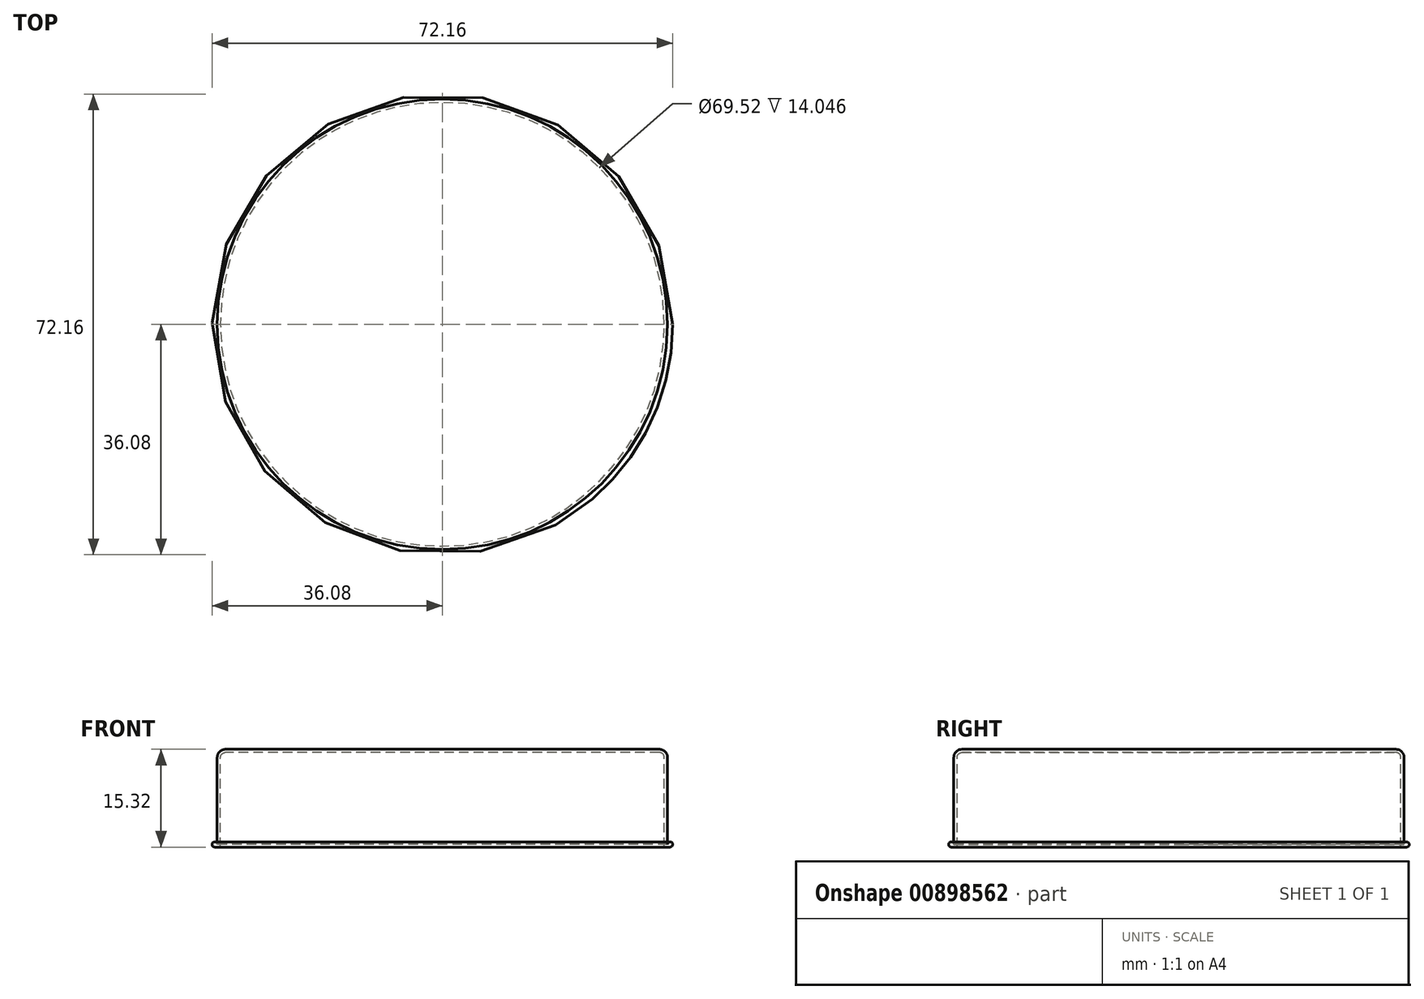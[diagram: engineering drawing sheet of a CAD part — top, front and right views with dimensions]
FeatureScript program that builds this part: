
annotation { "Feature Type Name" : "Feature", "Feature Type Description" : "" }
export const myFeature = defineFeature(function(context is Context, id is Id, definition is map)
    precondition{}
    {
        {
            var Q0;
            Q0=qCreatedBy(makeId("Front.planeOp"),FACE);
            var sketch = newSketch(context, id + "F0", { "sketchPlane" : qUnion([Q0])});
            skLineSegment(sketch, "E0", {"start": v(0, 0) * mm, "end": v(34, 0) * mm});
            skLineSegment(sketch, "E1", {"start": v(35.27, -1.27) * mm, "end": v(35.27, -14.9) * mm});
            skLineSegment(sketch, "E2.0", {"start": v(34.76, -1.27) * mm, "end": v(34.76, -15.32) * mm});
            skLineSegment(sketch, "E2.1", {"start": v(0, -0.5) * mm, "end": v(34, -0.5) * mm});
            skPoint(sketch, "E3.orphan", {"position": v(-76.06, 0) * mm});
            skLineSegment(sketch, "E4", {"start": v(35.67, -15.32) * mm, "end": v(34.76, -15.32) * mm});
            skArc(sketch, "E5", {"start": v(35.67, -15.32) * mm, "mid": v(35.96, -14.62) * mm, "end": v(35.27, -14.9) * mm});
            skPoint(sketch, "E6.orphan", {"position": v(35.27, -15.32) * mm});
            skPoint(sketch, "E7.visualSharp", {"position": v(34.76, -0.5) * mm});
            skArc(sketch, "E7.filletArc", {"start": v(34.76, -1.27) * mm, "mid": v(34.54, -0.73) * mm, "end": v(34, -0.5) * mm});
            skArc(sketch, "E8.0", {"start": v(35.27, -1.27) * mm, "mid": v(34.9, -0.37) * mm, "end": v(34, 0) * mm});
            skPoint(sketch, "E9.orphan", {"position": v(35.27, 0) * mm});
            skLineSegment(sketch, "E10", {"start": v(0, 0) * mm, "end": v(0, -0.5) * mm});
            skSolve(sketch);
        }
        {
            var Q0;
            Q0=makeQuery(id+"F0.imprint","IMPRINT",FACE,{"disambiguationData":[TD([[makeQuery(id+"F0.imprint","IMPRINT",EDGE,{"derivedFrom":sQuery(id+"F0.wireOp",EDGE,"E0")}),-1.0]])]});
            var Q1;
            Q1=sQuery(id+"F0.wireOp",EDGE,"E10");
            revolve(context, id + "F1", {"surfaceOperationType" : NewSurfaceOperationType.NEW, "entities" : qUnion([Q0]), "axis" : qUnion([Q1]), "revolveType" : RevolveType.FULL});
        }
    });
